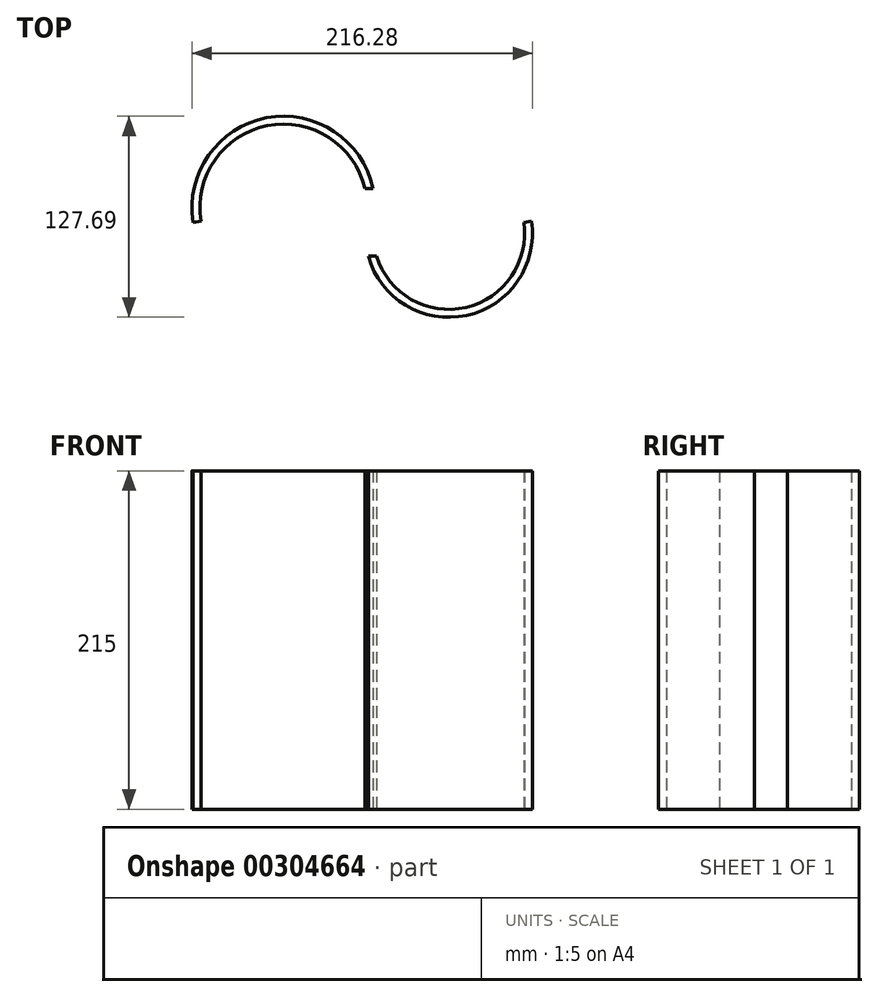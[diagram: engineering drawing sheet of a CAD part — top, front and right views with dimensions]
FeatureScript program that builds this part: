
annotation { "Feature Type Name" : "Feature", "Feature Type Description" : "" }
export const myFeature = defineFeature(function(context is Context, id is Id, definition is map)
    precondition{}
    {
        {
            var Q0;
            Q0=qCreatedBy(makeId("Top.planeOp"),FACE);
            var sketch = newSketch(context, id + "F0", { "sketchPlane" : qUnion([Q0])});
            skPoint(sketch, "E0.middle", {"position": v(0, 0) * mm});
            skPoint(sketch, "E1.endSnap0", {"position": v(105, 0) * mm});
            skArc(sketch, "E2", {"start": v(0, 0) * mm, "mid": v(-52.5, 61.63) * mm, "end": v(-105, 0) * mm});
            skArc(sketch, "E3", {"start": v(0, 0) * mm, "mid": v(52.5, -61.06) * mm, "end": v(105, 0) * mm});
            skArc(sketch, "E4.0", {"start": v(4.94, -0.77) * mm, "mid": v(-52.51, 66.63) * mm, "end": v(-109.94, -0.8) * mm});
            skArc(sketch, "E4.1", {"start": v(4.94, -0.77) * mm, "mid": v(52.51, -56.06) * mm, "end": v(100.06, -0.75) * mm});
            skLineSegment(sketch, "E5", {"start": v(-109.94, -0.8) * mm, "end": v(-105, 0) * mm});
            skLineSegment(sketch, "E6", {"start": v(100.06, -0.75) * mm, "end": v(105, 0) * mm});
            skSolve(sketch);
        }
        {
            var Q0;
            Q0 = qSketchRegion(id + "F0", true);
            extrude(context, id + "F1", {"entities" : qUnion([Q0]), "depth" : 215 * mm});
        }
        {
            var Q0;
            Q0=qCreatedBy(makeId("Right.planeOp"),FACE);
            var sketch = newSketch(context, id + "F2", { "sketchPlane" : qUnion([Q0])});
            skLineSegment(sketch, "E7.bottom", {"start": v(20.73, 0) * mm, "end": v(-22.27, 0) * mm});
            skLineSegment(sketch, "E7.top", {"start": v(20.73, 215) * mm, "end": v(-22.27, 215) * mm});
            skLineSegment(sketch, "E7.left", {"start": v(20.73, 0) * mm, "end": v(20.73, 215) * mm});
            skLineSegment(sketch, "E7.right", {"start": v(-22.27, 0) * mm, "end": v(-22.27, 215) * mm});
            skSolve(sketch);
        }
        {
            var Q0;
            Q0=makeQuery(id+"F2.imprint","IMPRINT",FACE,{"disambiguationData":[TD([[makeQuery(id+"F2.imprint","IMPRINT",EDGE,{"derivedFrom":sQuery(id+"F2.wireOp",EDGE,"E7.bottom")}),-1.0]])]});
            extrude(context, id + "F3", {"entities" : qUnion([Q0]), "operationType" : NewBodyOperationType.REMOVE, "depth" : 7 * mm, "hasSecondDirection" : true, "secondDirectionOppositeDirection" : true, "secondDirectionDepth" : 7 * mm});
        }
    });
